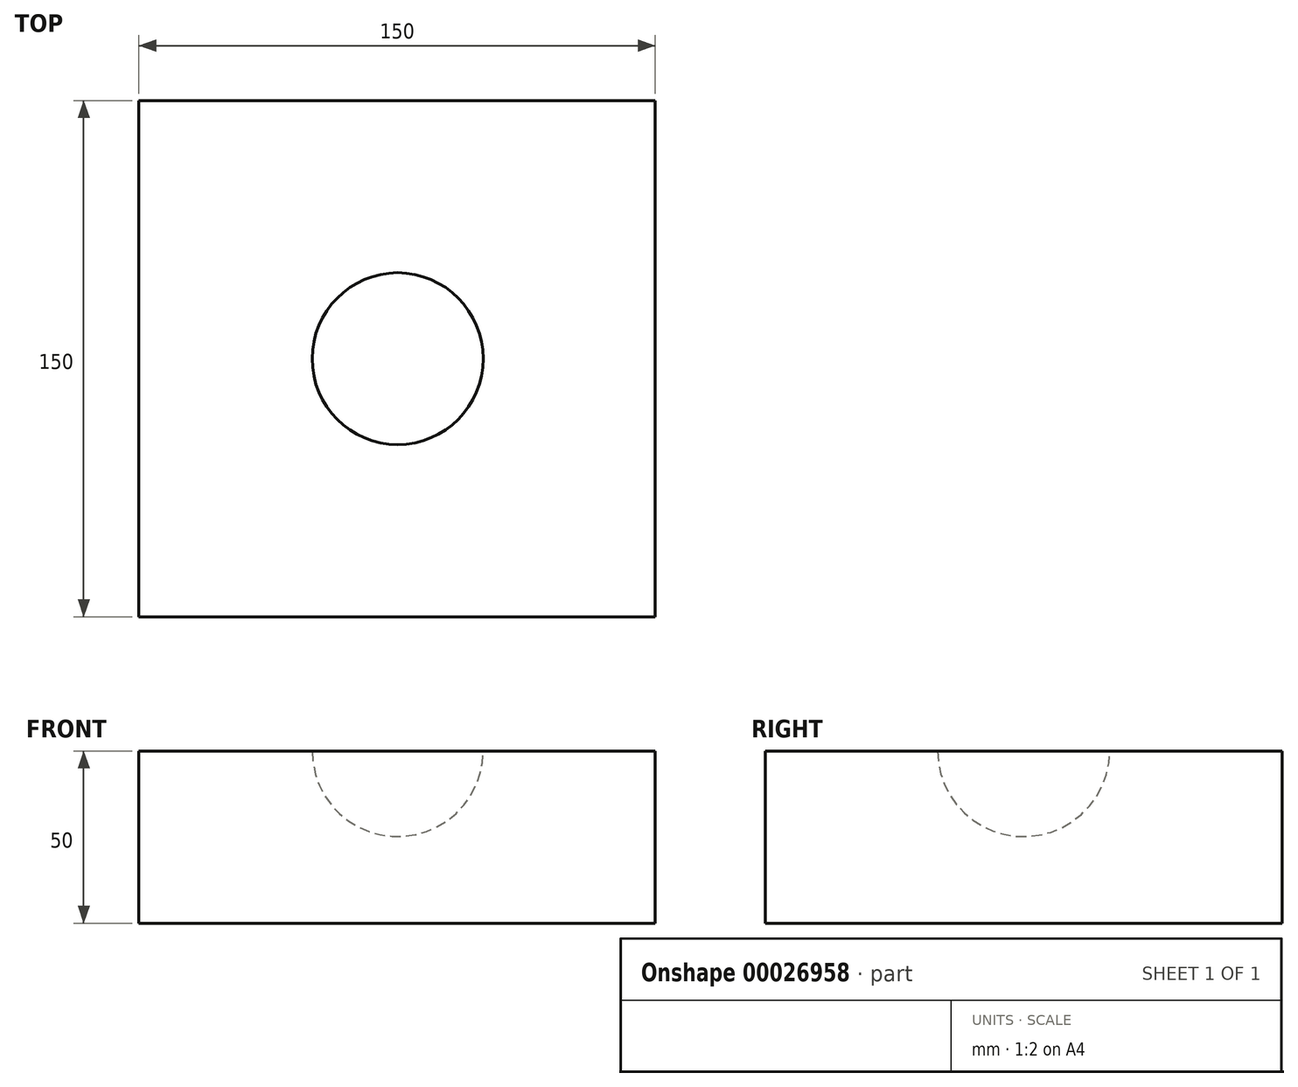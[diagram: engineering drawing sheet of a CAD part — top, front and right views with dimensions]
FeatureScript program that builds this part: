
annotation { "Feature Type Name" : "Feature", "Feature Type Description" : "" }
export const myFeature = defineFeature(function(context is Context, id is Id, definition is map)
    precondition{}
    {
        {
            var Q0;
            Q0=qCreatedBy(makeId("Top.planeOp"),FACE);
            var sketch = newSketch(context, id + "F0", { "sketchPlane" : qUnion([Q0])});
            skLineSegment(sketch, "E0.bottom", {"start": v(-16.94, 141.32) * mm, "end": v(133.06, 141.32) * mm});
            skLineSegment(sketch, "E0.top", {"start": v(-16.94, -8.68) * mm, "end": v(133.06, -8.68) * mm});
            skLineSegment(sketch, "E0.left", {"start": v(-16.94, 141.32) * mm, "end": v(-16.94, -8.68) * mm});
            skLineSegment(sketch, "E0.right", {"start": v(133.06, 141.32) * mm, "end": v(133.06, -8.68) * mm});
            skSolve(sketch);
        }
        {
            var Q0;
            Q0=makeQuery(id+"F0.imprint","IMPRINT",FACE,{"disambiguationData":[TD([[makeQuery(id+"F0.imprint","IMPRINT",EDGE,{"derivedFrom":sQuery(id+"F0.wireOp",EDGE,"E0.bottom")}),-1.0]])]});
            extrude(context, id + "F1", {"entities" : qUnion([Q0]), "depth" : 50 * mm});
        }
        {
            var Q0;
            Q0=makeQuery(id+"F1.opExtrude","CAP_FACE",FACE,{"disambiguationData":[OSD([sQuery(id+"F0.wireOp",EDGE,"E0.bottom"),sQuery(id+"F0.wireOp",EDGE,"E0.top"),sQuery(id+"F0.wireOp",EDGE,"E0.left"),sQuery(id+"F0.wireOp",EDGE,"E0.right")])],"isStart":false});
            var sketch = newSketch(context, id + "F2", { "sketchPlane" : qUnion([Q0])});
            skArc(sketch, "E1", {"start": v(58.23, 41.32) * mm, "mid": v(83.06, 66.32) * mm, "end": v(58.23, 91.32) * mm});
            skLineSegment(sketch, "E2", {"start": v(58.23, 91.32) * mm, "end": v(58.23, 41.32) * mm});
            skSolve(sketch);
        }
        {
            var Q0;
            Q0 = qSketchRegion(id + "F2", true);
            var Q1;
            Q1=sQuery(id+"F2.wireOp",EDGE,"E2");
            revolve(context, id + "F3", {"operationType" : NewBodyOperationType.REMOVE, "entities" : qUnion([Q0]), "axis" : qUnion([Q1]), "revolveType" : RevolveType.FULL, "oppositeDirection" : true});
        }
    });
